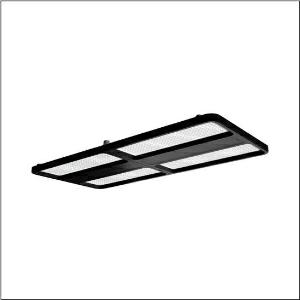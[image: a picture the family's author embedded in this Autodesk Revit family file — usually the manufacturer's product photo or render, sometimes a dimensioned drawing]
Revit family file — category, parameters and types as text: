
# Revit family: highbay_21_maxi_52hn31db4mda
name_source: partatom
category: Lighting Fixtures
units: mm (PartAtom-declared; Revit-internal decimal feet)

## family parameters
Cut with Voids When Loaded = No
Host = Face
Light Source = No
Part Type = Normal
Room Calculation Point = No
Round Connector Dimension = Use Diameter
Shared = No

## types (1)
- --- (1 x LED, 4230 lm, 22.6 W, 4000K)
    Apparent Load = 23 VA
    CIE Flux Codes = 89 97 99 100 100
    Color Rendering = 80
    Color Temperature = 4000K
    Default Elevation = 1800 mm
    Description = high bay luminaire Highbay 21 maxi; direct symmetric narrow distribution, light control with lens of PMMA; UGR ≤ 19 (X = 4H | Y = 8H | S = 0.25H | reflection values 70/50/20); luminous flux: 28.000lm; light colour: 840, colour temperature: 4000K, MacAdam ≤ 3 SDCM (initial), colour rendering: CRI > 80; luminous efficacy: 194,4lm/W; rated service life: 75.000h (L80) at AT= ta max; control: DALI 2; luminaire connection: terminal, 5-pole, max. 2.5mm² (cable entry for one cable, Ø 8.5..16mm); mains connection: 230..240V, AC/DC 0/50..60Hz; connected load: 144W; protection rating (complete): IP66; insulation class (complete): insulation class I (protective earthing); protection symbol: D; impact resistance: IK08; certification: CE, ENEC, VDE, UKCA; luminaire for central battery installations according to EN 60598-2-22, internal wiring halogen-free; luminaire LABS conformity tested according to VDMA 24364:2018-05; Suitable for use in the food industry according to the specifications of IFS-Food, HACCP and/or BRC; housing frame of high-performance plastic PA6, matt jet black (RAL 9005); cover of PMMA; dimension (LxWxH): 946 x 442 x 72mm; permissible operating ambient temperature: -40..+65°C (reducing of maximum allowable ambient temperature of 5°C with ceiling mounting); packaging unit: 1 piece; (delivery without accessories; please order mounting accessories separately)
    Height = 72 mm  [stored 0.23622 ft]
    Lamp = 1 x LED
    Lamp Light Flux = 4230 lm
    Lamp Power = 22.6 W
    Lamp count = 1
    Length = 946 mm
    Luminous efficacy = 187 lm/W
    Manufacturer = Siteco
    ModVariant = No
    Model = 52HN31DB4MDA
    Mounting Place = Ceiling
    Mounting Type = Pendant
    Number of Poles = 1
    OnlyDefault = Yes
    Power Factor = 1
    Product Name = Highbay 21 maxi
    Product group = high bay luminaire
    ProductGroupID = 902
    Protection Class = Protection class I
    Protection Degree = IP 66
    RLX_Detail_Level = 1
    RLX_Emergency_Light_Flux = 0 lm
    RLX_Emergency_Type = 0
    RLX_Emergency_Type_DB = No
    RlxData = <blob elided: 133137 chars, md5=443ba50f>
    Socket = socket
    Standby Power = 0 W
    System Light Flux = 4230 lm
    System Power = 23 W
    Type Comments = : DC mode (central or group accumulator) initial emergency light level
    Type Image = l_1378821.jpg
    URL = http://relux.com
    VarID = @adj_017773
    Voltage = 0 V
    Weight = 0.00 kg
    Width = 442 mm

note: [stored X ft] marks values corroborated as IEEE doubles in the binary element streams (Revit-internal decimal feet)

## geometry (parser evidence)
native form markers: Blend x4, Sweep x12
no freeform markers — native parametric forms only
